annotation { "Feature Type Name" : "Feature", "Feature Type Description" : "" }
export const myFeature = defineFeature(function(context is Context, id is Id, definition is map)
    precondition{}
    {
        {
            var Q0;
            Q0=qCreatedBy(makeId("Front.planeOp"),FACE);
            var sketch = newSketch(context, id + "F0", { "sketchPlane" : qUnion([Q0])});
            skLineSegment(sketch, "E0", {"start": v(-43.84, 62.94) * mm, "end": v(-43.84, 25.6) * mm});
            skArc(sketch, "E1", {"start": v(-52.23, 15.2) * mm, "mid": v(-46.2, 18.92) * mm, "end": v(-43.84, 25.6) * mm});
            skArc(sketch, "E2", {"start": v(-64.38, 23.58) * mm, "mid": v(-60.44, 16.3) * mm, "end": v(-52.23, 15.2) * mm});
            skLineSegment(sketch, "E3", {"start": v(-64.38, 23.58) * mm, "end": v(-64.55, 30.23) * mm});
            skLineSegment(sketch, "E4", {"start": v(-64.55, 30.23) * mm, "end": v(-58.33, 30.39) * mm});
            skLineSegment(sketch, "E5", {"start": v(-58.33, 30.39) * mm, "end": v(-58.33, 23.8) * mm});
            skPoint(sketch, "E6.end.orphan", {"position": v(-52.23, 19.53) * mm});
            skArc(sketch, "E7", {"start": v(-58.33, 23.8) * mm, "mid": v(-56.4, 20.08) * mm, "end": v(-52.23, 19.53) * mm});
            skLineSegment(sketch, "E8", {"start": v(-52.23, 19.53) * mm, "end": v(-52.23, 62.65) * mm});
            skLineSegment(sketch, "E9", {"start": v(-52.23, 62.65) * mm, "end": v(-62.07, 62.65) * mm});
            skLineSegment(sketch, "E10", {"start": v(-43.84, 62.94) * mm, "end": v(-34.58, 62.94) * mm});
            skLineSegment(sketch, "E11", {"start": v(-34.58, 62.94) * mm, "end": v(-34.58, 68.72) * mm});
            skLineSegment(sketch, "E12", {"start": v(-62.07, 62.65) * mm, "end": v(-62.07, 68.72) * mm});
            skLineSegment(sketch, "E13", {"start": v(-62.07, 68.72) * mm, "end": v(-34.58, 68.72) * mm});
            skLineSegment(sketch, "E14", {"start": v(-52.23, 15.2) * mm, "end": v(-49.76, 16.06) * mm});
            skArc(sketch, "E15", {"start": v(-53.4, 14.87) * mm, "mid": v(-53.59, 15.04) * mm, "end": v(-53.78, 15.2) * mm});
            skPoint(sketch, "E16.orphan", {"position": v(-58.28, 15.2) * mm});
            skLineSegment(sketch, "E17", {"start": v(-12.3, 66.7) * mm, "end": v(-29.37, 14.61) * mm});
            skLineSegment(sketch, "E18", {"start": v(-29.37, 14.61) * mm, "end": v(-16.06, 14.61) * mm});
            skLineSegment(sketch, "E19", {"start": v(-16.06, 14.61) * mm, "end": v(-9.4, 35.45) * mm});
            skLineSegment(sketch, "E20", {"start": v(-9.4, 35.45) * mm, "end": v(0, 35.45) * mm});
            skLineSegment(sketch, "E21", {"start": v(0, 35.45) * mm, "end": v(7.72, 14.98) * mm});
            skLineSegment(sketch, "E22", {"start": v(7.72, 14.98) * mm, "end": v(16.69, 14.98) * mm});
            skLineSegment(sketch, "E23", {"start": v(16.69, 14.98) * mm, "end": v(21.32, 14.98) * mm});
            skLineSegment(sketch, "E24", {"start": v(21.32, 14.98) * mm, "end": v(4.85, 67.26) * mm});
            skLineSegment(sketch, "E25", {"start": v(4.85, 67.26) * mm, "end": v(-12.3, 66.7) * mm});
            skPoint(sketch, "E26.end.orphan", {"position": v(0, 44.7) * mm});
            skPoint(sketch, "E26.start.orphan", {"position": v(-12.3, 44.7) * mm});
            skLineSegment(sketch, "E27", {"start": v(71.05, 63.77) * mm, "end": v(61.38, 63.77) * mm});
            skArc(sketch, "E28", {"start": v(61.38, 63.77) * mm, "mid": v(43.52, 54.42) * mm, "end": v(41.03, 34.42) * mm});
            skArc(sketch, "E29", {"start": v(41.03, 34.42) * mm, "mid": v(43.04, 23.8) * mm, "end": v(50.18, 15.67) * mm});
            skArc(sketch, "E30", {"start": v(50.18, 15.67) * mm, "mid": v(54.95, 13.62) * mm, "end": v(60.04, 14.61) * mm});
            skArc(sketch, "E31", {"start": v(60.04, 14.61) * mm, "mid": v(65.67, 16.04) * mm, "end": v(68.72, 20.98) * mm});
            skLineSegment(sketch, "E32", {"start": v(71.05, 63.77) * mm, "end": v(71.05, 58.59) * mm});
            skArc(sketch, "E33", {"start": v(71.05, 58.59) * mm, "mid": v(57.68, 57.8) * mm, "end": v(47.31, 49.34) * mm});
            skArc(sketch, "E34", {"start": v(47.31, 34.87) * mm, "mid": v(47.83, 27.39) * mm, "end": v(49.63, 20.11) * mm});
            skArc(sketch, "E35", {"start": v(49.63, 20.11) * mm, "mid": v(56.28, 17.08) * mm, "end": v(62.94, 20.11) * mm});
            skLineSegment(sketch, "E36", {"start": v(62.94, 20.11) * mm, "end": v(65.67, 28.46) * mm});
            skLineSegment(sketch, "E37", {"start": v(68.72, 20.98) * mm, "end": v(70, 28.46) * mm});
            skLineSegment(sketch, "E38", {"start": v(70, 28.46) * mm, "end": v(65.67, 28.46) * mm});
            skLineSegment(sketch, "E39", {"start": v(47.31, 34.87) * mm, "end": v(47.31, 49.34) * mm});
            skLineSegment(sketch, "E40", {"start": v(-9.52, 45.18) * mm, "end": v(-6.75, 52.02) * mm});
            skLineSegment(sketch, "E41", {"start": v(0, 44.7) * mm, "end": v(-2.69, 51.7) * mm});
            skLineSegment(sketch, "E42", {"start": v(-9.52, 45.18) * mm, "end": v(0, 45.18) * mm});
            skLineSegment(sketch, "E43", {"start": v(-6.75, 52.02) * mm, "end": v(-2.69, 51.7) * mm});
            skLineSegment(sketch, "E44", {"start": v(-91.37, 41.77) * mm, "end": v(-91.37, 8.73) * mm});
            skLineSegment(sketch, "E45", {"start": v(-91.37, 8.73) * mm, "end": v(-83.07, 8.73) * mm});
            skLineSegment(sketch, "E46", {"start": v(-83.07, 8.73) * mm, "end": v(-83.07, 18.5) * mm});
            skLineSegment(sketch, "E47", {"start": v(-83.07, 18.5) * mm, "end": v(-76.56, 8.25) * mm});
            skLineSegment(sketch, "E48", {"start": v(-76.56, 8.25) * mm, "end": v(-71.03, 8.25) * mm});
            skLineSegment(sketch, "E49", {"start": v(-71.03, 8.25) * mm, "end": v(-81.12, 26.3) * mm});
            skLineSegment(sketch, "E50", {"start": v(-81.12, 26.3) * mm, "end": v(-72.98, 41.28) * mm});
            skLineSegment(sketch, "E51", {"start": v(-72.98, 41.28) * mm, "end": v(-80.95, 41.28) * mm});
            skLineSegment(sketch, "E52", {"start": v(-80.95, 41.28) * mm, "end": v(-85.67, 28.75) * mm});
            skLineSegment(sketch, "E53", {"start": v(-85.67, 28.75) * mm, "end": v(-85.67, 41.77) * mm});
            skLineSegment(sketch, "E54", {"start": v(-85.67, 41.77) * mm, "end": v(-91.37, 41.77) * mm});
            skLineSegment(sketch, "E55", {"start": v(-77.7, -22.26) * mm, "end": v(-71.26, -33.56) * mm});
            skLineSegment(sketch, "E56", {"start": v(-71.26, -33.56) * mm, "end": v(-63.85, -33.56) * mm});
            skLineSegment(sketch, "E57", {"start": v(-85.49, -8.22) * mm, "end": v(-75.55, -8.22) * mm});
            skLineSegment(sketch, "E58", {"start": v(-75.55, -8.22) * mm, "end": v(-68, -21.5) * mm});
            skLineSegment(sketch, "E59", {"start": v(-63.85, -33.56) * mm, "end": v(-63.85, -7.47) * mm});
            skLineSegment(sketch, "E60", {"start": v(-68, -21.5) * mm, "end": v(-68, -7.47) * mm});
            skLineSegment(sketch, "E61", {"start": v(-68, -7.47) * mm, "end": v(-63.85, -7.47) * mm});
            skLineSegment(sketch, "E62", {"start": v(-85.49, -8.22) * mm, "end": v(-85.49, -33.56) * mm});
            skLineSegment(sketch, "E63", {"start": v(-77.7, -22.26) * mm, "end": v(-77.7, -33.56) * mm});
            skLineSegment(sketch, "E64", {"start": v(-77.7, -33.56) * mm, "end": v(-85.49, -33.56) * mm});
            skLineSegment(sketch, "E65", {"start": v(-57.42, -9.4) * mm, "end": v(-49.63, -33.17) * mm});
            skLineSegment(sketch, "E66", {"start": v(-49.63, -33.17) * mm, "end": v(-43.58, -21.09) * mm});
            skLineSegment(sketch, "E67", {"start": v(-43.58, -21.09) * mm, "end": v(-35.98, -33.95) * mm});
            skLineSegment(sketch, "E68", {"start": v(-35.98, -33.95) * mm, "end": v(-29.16, -9.4) * mm});
            skLineSegment(sketch, "E69", {"start": v(-57.42, -9.4) * mm, "end": v(-53.9, -8.24) * mm});
            skLineSegment(sketch, "E70", {"start": v(-53.9, -8.24) * mm, "end": v(-49.7, -21.1) * mm});
            skLineSegment(sketch, "E71", {"start": v(-49.7, -21.1) * mm, "end": v(-43.58, -14.66) * mm});
            skLineSegment(sketch, "E72", {"start": v(-43.58, -14.66) * mm, "end": v(-36.78, -21.1) * mm});
            skLineSegment(sketch, "E73", {"start": v(-36.78, -21.1) * mm, "end": v(-33.53, -9.4) * mm});
            skLineSegment(sketch, "E74", {"start": v(-33.53, -9.4) * mm, "end": v(-29.16, -9.4) * mm});
            skSolve(sketch);
        }
        {
            var Q0;
            Q0 = qSketchRegion(id + "F0", true);
            extrude(context, id + "F1", {"entities" : qUnion([Q0]), "depth" : 2.54 * mm});
        }
        {
            var Q0;
            Q0=makeQuery(id+"F1.opExtrude","CAP_FACE",FACE,{"disambiguationData":[OSD([sQuery(id+"F0.wireOp",EDGE,"E27"),sQuery(id+"F0.wireOp",EDGE,"E28"),sQuery(id+"F0.wireOp",EDGE,"E29"),sQuery(id+"F0.wireOp",EDGE,"E30"),sQuery(id+"F0.wireOp",EDGE,"E31"),sQuery(id+"F0.wireOp",EDGE,"E32"),sQuery(id+"F0.wireOp",EDGE,"E33"),sQuery(id+"F0.wireOp",EDGE,"E34"),sQuery(id+"F0.wireOp",EDGE,"E35"),sQuery(id+"F0.wireOp",EDGE,"E36"),sQuery(id+"F0.wireOp",EDGE,"E37"),sQuery(id+"F0.wireOp",EDGE,"E38"),sQuery(id+"F0.wireOp",EDGE,"E39")])],"isStart":false});
            var sketch = newSketch(context, id + "F2", { "sketchPlane" : qUnion([Q0])});
            skLineSegment(sketch, "E75", {"start": v(3.4, -15.33) * mm, "end": v(3.4, -42.24) * mm});
            skLineSegment(sketch, "E76", {"start": v(3.4, -42.24) * mm, "end": v(21.13, -42.24) * mm});
            skLineSegment(sketch, "E77", {"start": v(21.13, -42.24) * mm, "end": v(21.13, -36.58) * mm});
            skLineSegment(sketch, "E78", {"start": v(21.13, -36.58) * mm, "end": v(10.21, -36.58) * mm});
            skLineSegment(sketch, "E79", {"start": v(10.21, -36.58) * mm, "end": v(10.21, -15.33) * mm});
            skLineSegment(sketch, "E80", {"start": v(10.21, -15.33) * mm, "end": v(3.4, -15.33) * mm});
            skText(sketch, "E81", { "text": "JACKSON DOWNEY", "fontName": "OpenSans-Regular.ttf"});
            const initialGuessF2  = {"E81": [-0.068, -0.11536, 1, 0, 0.04087]};
            skSetInitialGuess(sketch, initialGuessF2);
            skSolve(sketch);
        }
        {
            var Q0;
            Q0=makeQuery(id+"F2.imprint","IMPRINT",FACE,{"disambiguationData":[TD([[makeQuery(id+"F2.imprint","IMPRINT",EDGE,{"derivedFrom":sQuery(id+"F2.wireOp",EDGE,"E75")}),1.0]])]});
            extrude(context, id + "F3", {"entities" : qUnion([Q0]), "depth" : 5.1 * mm});
        }
        {
            var Q0;
            Q0 = qSketchRegion(id + "F2", true);
            extrude(context, id + "F4", {"entities" : qUnion([Q0]), "operationType" : NewBodyOperationType.ADD, "depth" : 76.2 * mm});
        }
    });